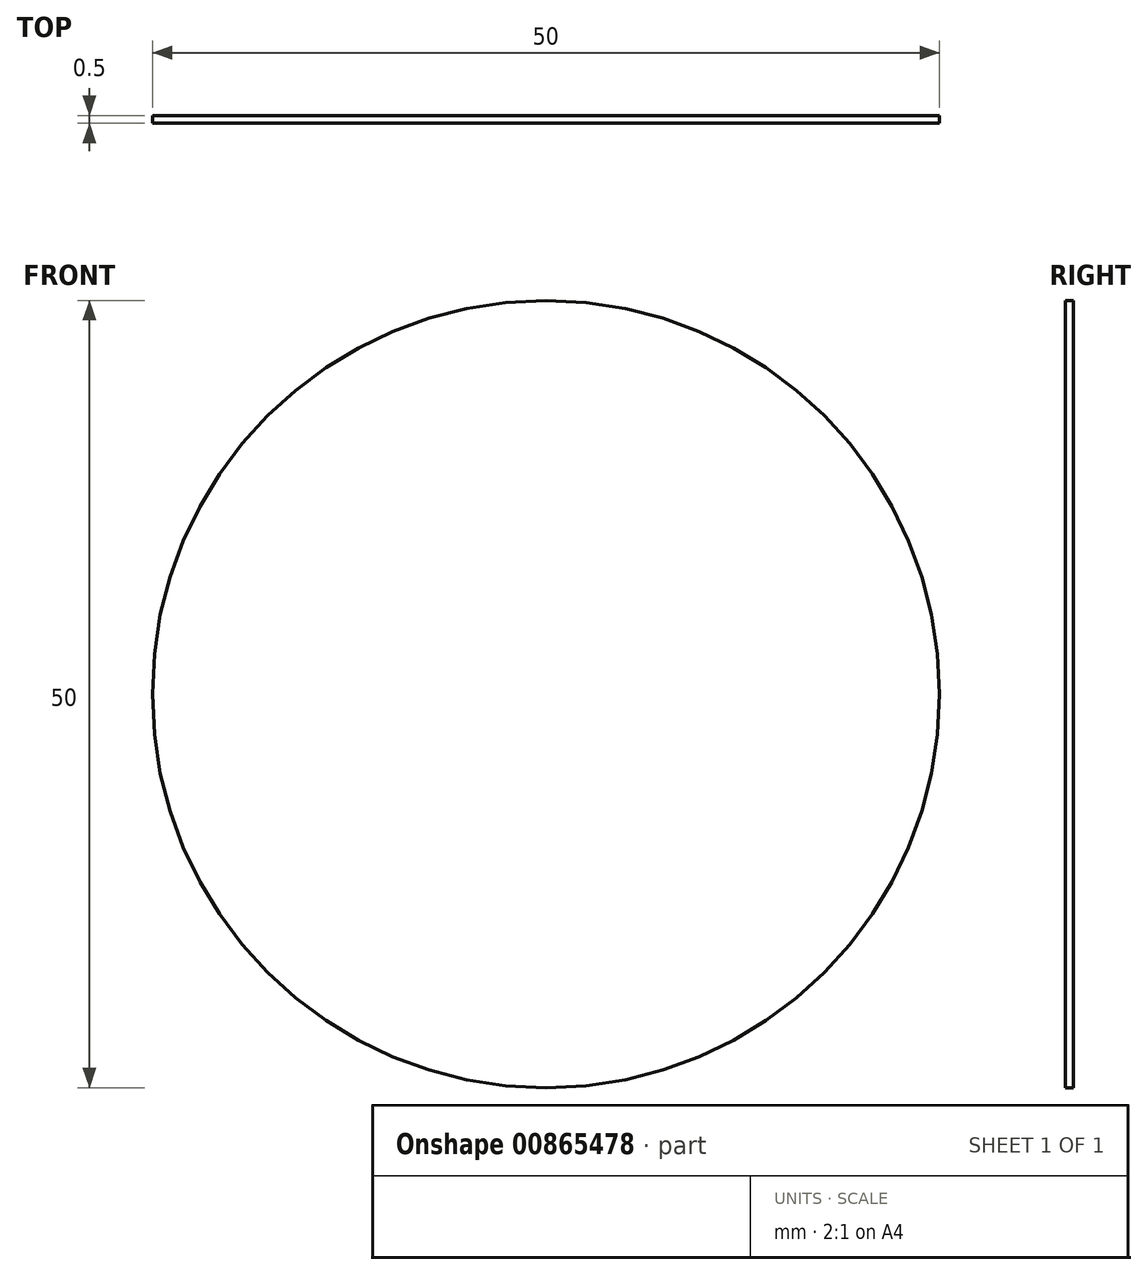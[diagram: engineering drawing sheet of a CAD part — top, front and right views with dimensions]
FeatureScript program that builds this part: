
annotation { "Feature Type Name" : "Feature", "Feature Type Description" : "" }
export const myFeature = defineFeature(function(context is Context, id is Id, definition is map)
    precondition{}
    {
        {
            var Q0;
            Q0=qCreatedBy(makeId("Front.planeOp"),FACE);
            var sketch = newSketch(context, id + "F0", { "sketchPlane" : qUnion([Q0])});
            skCircle(sketch, "E0", {"center": v(0, 0) * mm, "radius": 25 * mm});
            skSolve(sketch);
        }
        {
            var Q0;
            Q0 = qSketchRegion(id + "F0", true);
            extrude(context, id + "F1", {"entities" : qUnion([Q0]), "depth" : 0.5 * mm, "offsetDistance" : 25 * mm});
        }
    });
